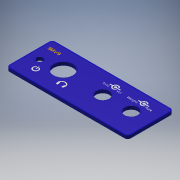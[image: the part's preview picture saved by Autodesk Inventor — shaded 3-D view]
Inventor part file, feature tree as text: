
AUTODESK INVENTOR PART (.ipt)
format: ipt  version: 2016 (Build 200138000, 138)  size: 200,192 bytes
history: native  units: mm
features: sketch x5, extrude x4, other x2, fillet x1
ambient origin geometry x8: Origin, YZ Plane, XZ Plane, XY Plane, X Axis, Y Axis, Z Axis, Center Point
bodies: Solid1 (feature_tree)
feature tree (12):
  extrude  "Extrusion1"  Depth=22.5mm
  fillet  "Fillet1"  Radius=1.6mm
  extrude  "Extrusion2"  Depth=1.5mm
  extrude  "Extrusion3"  Depth=10.0mm
  extrude  "Extrusion4"  Depth=11.51mm
  other  "Decal1"
  sketch  "Sketch1"  dims[d0=59.5mm d1=22.5mm d2=1.6mm d3=0.0mm]
  sketch  "Sketch2"  dims[d4=1.5mm d5=9.5mm]
  sketch  "Sketch3"  dims[d6=10.0mm d7=0.0mm d8=6.5mm]
  sketch  "Sketch4"  dims[d9=13.97mm d10=11.51mm]
  sketch  "Sketch5"  dims[d11=5.985mm d12=10.0mm d13=0.0mm d14=11.51mm d15=12.51mm d16=15.371mm d17=6.01mm d18=1.401mm d19=3.1mm d20=3.81mm d21=5.1mm d22=10.0mm d23=0.0mm]
  other  "Image1"
